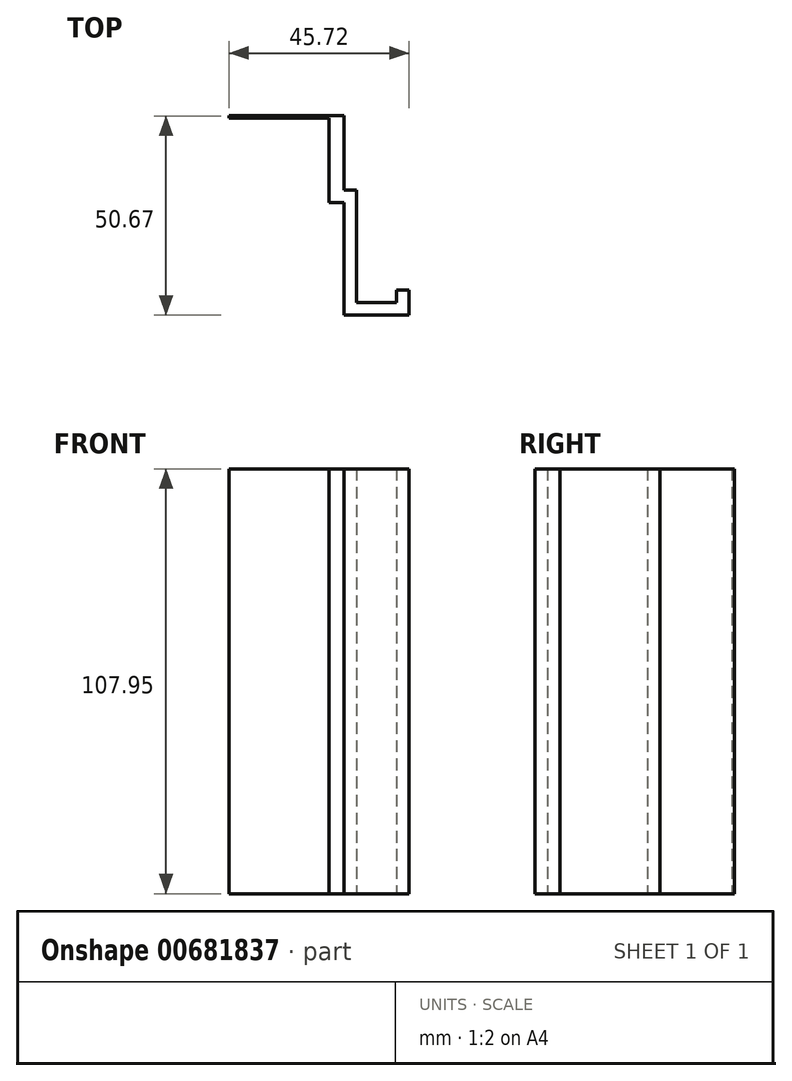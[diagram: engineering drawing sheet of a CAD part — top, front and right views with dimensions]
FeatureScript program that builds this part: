
annotation { "Feature Type Name" : "Feature", "Feature Type Description" : "" }
export const myFeature = defineFeature(function(context is Context, id is Id, definition is map)
    precondition{}
    {
        {
            var Q0;
            Q0=qCreatedBy(makeId("Top.planeOp"),FACE);
            var sketch = newSketch(context, id + "F0", { "sketchPlane" : qUnion([Q0])});
            skLineSegment(sketch, "E0", {"start": v(-49.1, 56) * mm, "end": v(-23.7, 56) * mm});
            skLineSegment(sketch, "E1", {"start": v(-23.7, 56) * mm, "end": v(-23.7, 55.37) * mm});
            skLineSegment(sketch, "E2", {"start": v(-23.7, 55.37) * mm, "end": v(-49.1, 55.37) * mm});
            skLineSegment(sketch, "E3", {"start": v(-49.1, 55.37) * mm, "end": v(-49.1, 56) * mm});
            skLineSegment(sketch, "E4", {"start": v(-23.7, 56) * mm, "end": v(-19.9, 56) * mm});
            skLineSegment(sketch, "E5", {"start": v(-19.9, 56) * mm, "end": v(-19.9, 55.37) * mm});
            skLineSegment(sketch, "E6", {"start": v(-19.9, 55.37) * mm, "end": v(-23.7, 55.37) * mm});
            skLineSegment(sketch, "E7", {"start": v(-19.9, 37.08) * mm, "end": v(-19.9, 55.37) * mm});
            skLineSegment(sketch, "E8", {"start": v(-19.9, 37.08) * mm, "end": v(-23.7, 37.08) * mm});
            skLineSegment(sketch, "E9", {"start": v(-23.7, 55.37) * mm, "end": v(-23.7, 37.08) * mm});
            skLineSegment(sketch, "E10", {"start": v(-19.9, 37.08) * mm, "end": v(-16.72, 37.08) * mm});
            skLineSegment(sketch, "E11", {"start": v(-19.9, 37.08) * mm, "end": v(-19.9, 33.9) * mm});
            skLineSegment(sketch, "E12", {"start": v(-19.9, 33.9) * mm, "end": v(-16.72, 33.9) * mm});
            skLineSegment(sketch, "E13", {"start": v(-16.72, 33.9) * mm, "end": v(-16.72, 37.08) * mm});
            skLineSegment(sketch, "E14", {"start": v(-23.7, 37.08) * mm, "end": v(-23.7, 33.9) * mm});
            skLineSegment(sketch, "E15", {"start": v(-23.7, 33.9) * mm, "end": v(-19.9, 33.9) * mm});
            skLineSegment(sketch, "E16", {"start": v(-19.9, 5.33) * mm, "end": v(-16.72, 5.33) * mm});
            skLineSegment(sketch, "E17", {"start": v(-6.56, 5.33) * mm, "end": v(-16.72, 5.33) * mm});
            skLineSegment(sketch, "E18", {"start": v(-3.38, 5.33) * mm, "end": v(-6.56, 5.33) * mm});
            skLineSegment(sketch, "E19", {"start": v(-6.56, 11.68) * mm, "end": v(-3.38, 11.68) * mm});
            skLineSegment(sketch, "E20", {"start": v(-16.72, 33.9) * mm, "end": v(-16.72, 8.5) * mm});
            skLineSegment(sketch, "E21", {"start": v(-16.72, 8.5) * mm, "end": v(-3.38, 8.5) * mm});
            skLineSegment(sketch, "E22", {"start": v(-3.38, 8.5) * mm, "end": v(-3.38, 11.68) * mm});
            skLineSegment(sketch, "E23", {"start": v(-19.9, 5.33) * mm, "end": v(-19.9, 8.5) * mm});
            skLineSegment(sketch, "E24", {"start": v(-19.9, 8.5) * mm, "end": v(-19.9, 33.9) * mm});
            skLineSegment(sketch, "E25", {"start": v(-6.56, 11.68) * mm, "end": v(-6.56, 8.5) * mm});
            skLineSegment(sketch, "E26", {"start": v(-3.38, 8.5) * mm, "end": v(-6.56, 8.5) * mm});
            skLineSegment(sketch, "E27", {"start": v(-16.72, 8.5) * mm, "end": v(-19.9, 8.5) * mm});
            skLineSegment(sketch, "E28", {"start": v(-3.38, 5.33) * mm, "end": v(-3.38, 8.5) * mm});
            skLineSegment(sketch, "E29", {"start": v(-16.72, 5.33) * mm, "end": v(-16.72, 8.5) * mm});
            skLineSegment(sketch, "E30", {"start": v(-6.56, 5.33) * mm, "end": v(-6.56, 8.5) * mm});
            skSolve(sketch);
        }
        {
            var Q0;
            Q0=makeQuery(id+"F0.imprint","IMPRINT",FACE,{"disambiguationData":[TD([[makeQuery(id+"F0.imprint","IMPRINT",EDGE,{"derivedFrom":sQuery(id+"F0.wireOp",EDGE,"E0")}),-1.0]])]});
            var Q1;
            Q1=makeQuery(id+"F0.imprint","IMPRINT",FACE,{"disambiguationData":[TD([[makeQuery(id+"F0.imprint","IMPRINT",EDGE,{"derivedFrom":sQuery(id+"F0.wireOp",EDGE,"E1")}),1.0]])]});
            var Q2;
            Q2=makeQuery(id+"F0.imprint","IMPRINT",FACE,{"disambiguationData":[TD([[makeQuery(id+"F0.imprint","IMPRINT",EDGE,{"derivedFrom":sQuery(id+"F0.wireOp",EDGE,"E6")}),1.0]])]});
            var Q3;
            Q3=makeQuery(id+"F0.imprint","IMPRINT",FACE,{"disambiguationData":[TD([[makeQuery(id+"F0.imprint","IMPRINT",EDGE,{"derivedFrom":sQuery(id+"F0.wireOp",EDGE,"E8")}),1.0]])]});
            var Q4;
            Q4=makeQuery(id+"F0.imprint","IMPRINT",FACE,{"disambiguationData":[TD([[makeQuery(id+"F0.imprint","IMPRINT",EDGE,{"derivedFrom":sQuery(id+"F0.wireOp",EDGE,"E10")}),-1.0]])]});
            var Q5;
            Q5=makeQuery(id+"F0.imprint","IMPRINT",FACE,{"disambiguationData":[TD([[makeQuery(id+"F0.imprint","IMPRINT",EDGE,{"derivedFrom":sQuery(id+"F0.wireOp",EDGE,"E12")}),-1.0]])]});
            var Q6;
            Q6=makeQuery(id+"F0.imprint","IMPRINT",FACE,{"disambiguationData":[TD([[makeQuery(id+"F0.imprint","IMPRINT",EDGE,{"derivedFrom":sQuery(id+"F0.wireOp",EDGE,"E16")}),1.0]])]});
            var Q7;
            Q7=makeQuery(id+"F0.imprint","IMPRINT",FACE,{"disambiguationData":[TD([[makeQuery(id+"F0.imprint","IMPRINT",EDGE,{"derivedFrom":sQuery(id+"F0.wireOp",EDGE,"E17")}),-1.0]])]});
            var Q8;
            Q8=makeQuery(id+"F0.imprint","IMPRINT",FACE,{"disambiguationData":[TD([[makeQuery(id+"F0.imprint","IMPRINT",EDGE,{"derivedFrom":sQuery(id+"F0.wireOp",EDGE,"E18")}),-1.0]])]});
            var Q9;
            Q9=makeQuery(id+"F0.imprint","IMPRINT",FACE,{"disambiguationData":[TD([[makeQuery(id+"F0.imprint","IMPRINT",EDGE,{"derivedFrom":sQuery(id+"F0.wireOp",EDGE,"E19")}),-1.0]])]});
            extrude(context, id + "F1", {"entities" : qUnion([Q0, Q1, Q2, Q3, Q4, Q5, Q6, Q7, Q8, Q9]), "depth" : 107.95 * mm, "offsetDistance" : 25.4 * mm});
        }
    });
